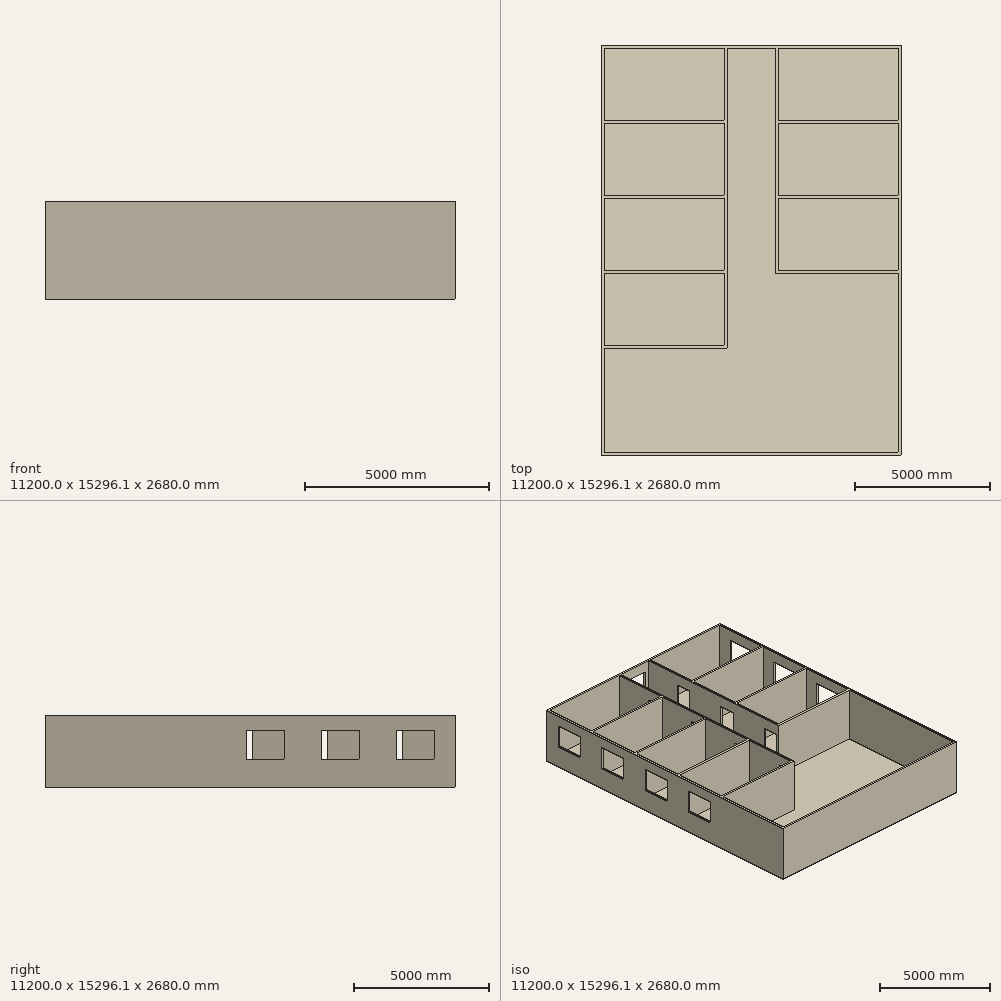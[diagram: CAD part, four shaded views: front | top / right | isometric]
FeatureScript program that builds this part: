
annotation { "Feature Type Name" : "Feature", "Feature Type Description" : "" }
export const myFeature = defineFeature(function(context is Context, id is Id, definition is map)
    precondition{}
    {
        {
            var Q0;
            Q0=qCreatedBy(makeId("Top.planeOp"),FACE);
            var sketch = newSketch(context, id + "F0", { "sketchPlane" : qUnion([Q0])});
            skLineSegment(sketch, "E0.bottom", {"start": v(4600, -100) * mm, "end": v(100, -100) * mm});
            skLineSegment(sketch, "E0.top", {"start": v(4600, -2800) * mm, "end": v(100, -2800) * mm});
            skLineSegment(sketch, "E0.left", {"start": v(4600, -100) * mm, "end": v(4600, -2800) * mm});
            skLineSegment(sketch, "E0.right", {"start": v(100, -100) * mm, "end": v(100, -2800) * mm});
            skLineSegment(sketch, "E1.bottom", {"start": v(4600, -2900) * mm, "end": v(100, -2900) * mm});
            skLineSegment(sketch, "E1.top", {"start": v(4600, -5600) * mm, "end": v(100, -5600) * mm});
            skLineSegment(sketch, "E1.left", {"start": v(4600, -2900) * mm, "end": v(4600, -5600) * mm});
            skLineSegment(sketch, "E1.right", {"start": v(100, -2900) * mm, "end": v(100, -5600) * mm});
            skLineSegment(sketch, "E2.bottom", {"start": v(11100, -100) * mm, "end": v(6600, -100) * mm});
            skLineSegment(sketch, "E2.top", {"start": v(11100, -2800) * mm, "end": v(6600, -2800) * mm});
            skLineSegment(sketch, "E2.left", {"start": v(11100, -100) * mm, "end": v(11100, -2800) * mm});
            skLineSegment(sketch, "E2.right", {"start": v(6600, -100) * mm, "end": v(6600, -2800) * mm});
            skLineSegment(sketch, "E3.bottom", {"start": v(11100, -2900) * mm, "end": v(6600, -2900) * mm});
            skLineSegment(sketch, "E3.top", {"start": v(11100, -5600) * mm, "end": v(6600, -5600) * mm});
            skLineSegment(sketch, "E3.left", {"start": v(11100, -2900) * mm, "end": v(11100, -5600) * mm});
            skLineSegment(sketch, "E3.right", {"start": v(6600, -2900) * mm, "end": v(6600, -5600) * mm});
            skLineSegment(sketch, "E4.bottom", {"start": v(4700, -100) * mm, "end": v(6500, -100) * mm});
            skLineSegment(sketch, "E5.bottom", {"start": v(0, 0) * mm, "end": v(11200, 0) * mm});
            skLineSegment(sketch, "E5.top", {"start": v(0, -15296.15) * mm, "end": v(11200, -15296.15) * mm});
            skLineSegment(sketch, "E5.left", {"start": v(0, 0) * mm, "end": v(0, -15296.15) * mm});
            skLineSegment(sketch, "E5.right", {"start": v(11200, 0) * mm, "end": v(11200, -15296.15) * mm});
            skLineSegment(sketch, "E6.bottom", {"start": v(4600, -5700) * mm, "end": v(100, -5700) * mm});
            skLineSegment(sketch, "E6.top", {"start": v(4600, -8400) * mm, "end": v(100, -8400) * mm});
            skLineSegment(sketch, "E6.left", {"start": v(4600, -5700) * mm, "end": v(4600, -8400) * mm});
            skLineSegment(sketch, "E6.right", {"start": v(100, -5700) * mm, "end": v(100, -8400) * mm});
            skLineSegment(sketch, "E7.bottom", {"start": v(11100, -5700) * mm, "end": v(6600, -5700) * mm});
            skLineSegment(sketch, "E7.top", {"start": v(11100, -8400) * mm, "end": v(6600, -8400) * mm});
            skLineSegment(sketch, "E7.left", {"start": v(11100, -5700) * mm, "end": v(11100, -8400) * mm});
            skLineSegment(sketch, "E7.right", {"start": v(6600, -5700) * mm, "end": v(6600, -8400) * mm});
            skLineSegment(sketch, "E8.bottom", {"start": v(4600, -8500) * mm, "end": v(100, -8500) * mm});
            skLineSegment(sketch, "E8.top", {"start": v(4600, -11200) * mm, "end": v(100, -11200) * mm});
            skLineSegment(sketch, "E8.left", {"start": v(4600, -8500) * mm, "end": v(4600, -11200) * mm});
            skLineSegment(sketch, "E8.right", {"start": v(100, -8500) * mm, "end": v(100, -11200) * mm});
            skLineSegment(sketch, "E9", {"start": v(6500, -8500) * mm, "end": v(6500, -100) * mm});
            skLineSegment(sketch, "E10", {"start": v(4700, -11300) * mm, "end": v(4700, -100) * mm});
            skLineSegment(sketch, "E11", {"start": v(6500, -8500) * mm, "end": v(11100, -8500) * mm});
            skLineSegment(sketch, "E12", {"start": v(11100, -8500) * mm, "end": v(11100, -15196.15) * mm});
            skLineSegment(sketch, "E13", {"start": v(11100, -15196.15) * mm, "end": v(100, -15196.15) * mm});
            skLineSegment(sketch, "E14", {"start": v(100, -15196.15) * mm, "end": v(100, -11300) * mm});
            skLineSegment(sketch, "E15", {"start": v(100, -11300) * mm, "end": v(4700, -11300) * mm});
            skLineSegment(sketch, "E16.bottom", {"start": v(4600, -2760) * mm, "end": v(4700, -2760) * mm});
            skLineSegment(sketch, "E16.top", {"start": v(4600, -1960) * mm, "end": v(4700, -1960) * mm});
            skLineSegment(sketch, "E16.left", {"start": v(4600, -2760) * mm, "end": v(4600, -1960) * mm});
            skLineSegment(sketch, "E16.right", {"start": v(4700, -2760) * mm, "end": v(4700, -1960) * mm});
            skLineSegment(sketch, "E17.bottom", {"start": v(6500, -2760) * mm, "end": v(6600, -2760) * mm});
            skLineSegment(sketch, "E17.top", {"start": v(6500, -1960) * mm, "end": v(6600, -1960) * mm});
            skLineSegment(sketch, "E17.left", {"start": v(6500, -2760) * mm, "end": v(6500, -1960) * mm});
            skLineSegment(sketch, "E17.right", {"start": v(6600, -2760) * mm, "end": v(6600, -1960) * mm});
            skLineSegment(sketch, "E18.bottom", {"start": v(6500, -5560) * mm, "end": v(6600, -5560) * mm});
            skLineSegment(sketch, "E18.top", {"start": v(6500, -4760) * mm, "end": v(6600, -4760) * mm});
            skLineSegment(sketch, "E18.left", {"start": v(6500, -5560) * mm, "end": v(6500, -4760) * mm});
            skLineSegment(sketch, "E18.right", {"start": v(6600, -5560) * mm, "end": v(6600, -4760) * mm});
            skLineSegment(sketch, "E19.bottom", {"start": v(4600, -5560) * mm, "end": v(4700, -5560) * mm});
            skLineSegment(sketch, "E19.top", {"start": v(4600, -4760) * mm, "end": v(4700, -4760) * mm});
            skLineSegment(sketch, "E19.left", {"start": v(4600, -5560) * mm, "end": v(4600, -4760) * mm});
            skLineSegment(sketch, "E19.right", {"start": v(4700, -5560) * mm, "end": v(4700, -4760) * mm});
            skLineSegment(sketch, "E20.bottom", {"start": v(4600, -8360) * mm, "end": v(4700, -8360) * mm});
            skLineSegment(sketch, "E20.top", {"start": v(4600, -7560) * mm, "end": v(4700, -7560) * mm});
            skLineSegment(sketch, "E20.left", {"start": v(4600, -8360) * mm, "end": v(4600, -7560) * mm});
            skLineSegment(sketch, "E20.right", {"start": v(4700, -8360) * mm, "end": v(4700, -7560) * mm});
            skLineSegment(sketch, "E21.bottom", {"start": v(6500, -8360) * mm, "end": v(6600, -8360) * mm});
            skLineSegment(sketch, "E21.top", {"start": v(6500, -7560) * mm, "end": v(6600, -7560) * mm});
            skLineSegment(sketch, "E21.left", {"start": v(6500, -8360) * mm, "end": v(6500, -7560) * mm});
            skLineSegment(sketch, "E21.right", {"start": v(6600, -8360) * mm, "end": v(6600, -7560) * mm});
            skLineSegment(sketch, "E22.bottom", {"start": v(4600, -11240) * mm, "end": v(4700, -11240) * mm});
            skLineSegment(sketch, "E22.top", {"start": v(4600, -10440) * mm, "end": v(4700, -10440) * mm});
            skLineSegment(sketch, "E22.left", {"start": v(4600, -11240) * mm, "end": v(4600, -10440) * mm});
            skLineSegment(sketch, "E22.right", {"start": v(4700, -11240) * mm, "end": v(4700, -10440) * mm});
            skSolve(sketch);
        }
        {
            var Q0;
            {var subQ38=sQuery(id+"F0.wireOp",EDGE,"E0.bottom");Q0=makeQuery(id+"F0.imprint","IMPRINT",FACE,{"disambiguationData":[TD([[makeQuery(id+"F0.imprint","IMPRINT",EDGE,{"derivedFrom":subQ38}),-1.0]])]});}
            extrude(context, id + "F1", {"entities" : qUnion([Q0]), "oppositeDirection" : true, "depth" : 2050 * mm, "offsetDistance" : 25 * mm});
        }
        {
            var Q0;
            {var subQ38=sQuery(id+"F0.wireOp",EDGE,"E0.bottom");Q0=makeQuery(id+"F0.imprint","IMPRINT",FACE,{"disambiguationData":[TD([[makeQuery(id+"F0.imprint","IMPRINT",EDGE,{"derivedFrom":subQ38}),-1.0]])]});}
            var Q1;
            Q1=makeQuery(id+"F0.imprint","IMPRINT",FACE,{"disambiguationData":[TD([[makeQuery(id+"F0.imprint","IMPRINT",EDGE,{"derivedFrom":sQuery(id+"F0.wireOp",EDGE,"E17.bottom")}),1.0]])]});
            var Q2;
            Q2=makeQuery(id+"F0.imprint","IMPRINT",FACE,{"disambiguationData":[TD([[makeQuery(id+"F0.imprint","IMPRINT",EDGE,{"derivedFrom":sQuery(id+"F0.wireOp",EDGE,"E18.bottom")}),1.0]])]});
            var Q3;
            Q3=makeQuery(id+"F0.imprint","IMPRINT",FACE,{"disambiguationData":[TD([[makeQuery(id+"F0.imprint","IMPRINT",EDGE,{"derivedFrom":sQuery(id+"F0.wireOp",EDGE,"E22.bottom")}),1.0]])]});
            var Q4;
            Q4=makeQuery(id+"F0.imprint","IMPRINT",FACE,{"disambiguationData":[TD([[makeQuery(id+"F0.imprint","IMPRINT",EDGE,{"derivedFrom":sQuery(id+"F0.wireOp",EDGE,"E21.bottom")}),1.0]])]});
            var Q5;
            Q5=makeQuery(id+"F0.imprint","IMPRINT",FACE,{"disambiguationData":[TD([[makeQuery(id+"F0.imprint","IMPRINT",EDGE,{"derivedFrom":sQuery(id+"F0.wireOp",EDGE,"E20.bottom")}),1.0]])]});
            var Q6;
            Q6=makeQuery(id+"F0.imprint","IMPRINT",FACE,{"disambiguationData":[TD([[makeQuery(id+"F0.imprint","IMPRINT",EDGE,{"derivedFrom":sQuery(id+"F0.wireOp",EDGE,"E19.bottom")}),1.0]])]});
            var Q7;
            Q7=makeQuery(id+"F0.imprint","IMPRINT",FACE,{"disambiguationData":[TD([[makeQuery(id+"F0.imprint","IMPRINT",EDGE,{"derivedFrom":sQuery(id+"F0.wireOp",EDGE,"E16.bottom")}),1.0]])]});
            extrude(context, id + "F2", {"entities" : qUnion([Q0, Q1, Q2, Q3, Q4, Q5, Q6, Q7]), "operationType" : NewBodyOperationType.ADD, "depth" : 530 * mm, "offsetDistance" : 25 * mm});
        }
        {
            var Q0;
            Q0=makeQuery(id+"F1.opExtrude","CAP_FACE",FACE,{"disambiguationData":[OSD([sQuery(id+"F0.wireOp",EDGE,"E0.bottom"),sQuery(id+"F0.wireOp",EDGE,"E0.top"),sQuery(id+"F0.wireOp",EDGE,"E0.left"),sQuery(id+"F0.wireOp",EDGE,"E0.right"),sQuery(id+"F0.wireOp",EDGE,"E1.bottom"),sQuery(id+"F0.wireOp",EDGE,"E1.top"),sQuery(id+"F0.wireOp",EDGE,"E1.left"),sQuery(id+"F0.wireOp",EDGE,"E1.right"),sQuery(id+"F0.wireOp",EDGE,"E2.bottom"),sQuery(id+"F0.wireOp",EDGE,"E2.top"),sQuery(id+"F0.wireOp",EDGE,"E2.left"),sQuery(id+"F0.wireOp",EDGE,"E2.right"),sQuery(id+"F0.wireOp",EDGE,"E3.bottom"),sQuery(id+"F0.wireOp",EDGE,"E3.top"),sQuery(id+"F0.wireOp",EDGE,"E3.left"),sQuery(id+"F0.wireOp",EDGE,"E3.right"),sQuery(id+"F0.wireOp",EDGE,"E4.bottom"),sQuery(id+"F0.wireOp",EDGE,"E5.bottom"),sQuery(id+"F0.wireOp",EDGE,"E5.top"),sQuery(id+"F0.wireOp",EDGE,"E5.left"),sQuery(id+"F0.wireOp",EDGE,"E5.right"),sQuery(id+"F0.wireOp",EDGE,"E6.bottom"),sQuery(id+"F0.wireOp",EDGE,"E6.top"),sQuery(id+"F0.wireOp",EDGE,"E6.left"),sQuery(id+"F0.wireOp",EDGE,"E6.right"),sQuery(id+"F0.wireOp",EDGE,"E7.bottom"),sQuery(id+"F0.wireOp",EDGE,"E7.top"),sQuery(id+"F0.wireOp",EDGE,"E7.left"),sQuery(id+"F0.wireOp",EDGE,"E7.right"),sQuery(id+"F0.wireOp",EDGE,"E8.bottom"),sQuery(id+"F0.wireOp",EDGE,"E8.top"),sQuery(id+"F0.wireOp",EDGE,"E8.left"),sQuery(id+"F0.wireOp",EDGE,"E8.right"),sQuery(id+"F0.wireOp",EDGE,"E9"),sQuery(id+"F0.wireOp",EDGE,"E10"),sQuery(id+"F0.wireOp",EDGE,"E11"),sQuery(id+"F0.wireOp",EDGE,"E12"),sQuery(id+"F0.wireOp",EDGE,"E13"),sQuery(id+"F0.wireOp",EDGE,"E14"),sQuery(id+"F0.wireOp",EDGE,"E15"),sQuery(id+"F0.wireOp",EDGE,"E16.bottom"),sQuery(id+"F0.wireOp",EDGE,"E16.top"),sQuery(id+"F0.wireOp",EDGE,"E17.bottom"),sQuery(id+"F0.wireOp",EDGE,"E17.top"),sQuery(id+"F0.wireOp",EDGE,"E18.bottom"),sQuery(id+"F0.wireOp",EDGE,"E18.top"),sQuery(id+"F0.wireOp",EDGE,"E19.bottom"),sQuery(id+"F0.wireOp",EDGE,"E19.top"),sQuery(id+"F0.wireOp",EDGE,"E20.bottom"),sQuery(id+"F0.wireOp",EDGE,"E20.top"),sQuery(id+"F0.wireOp",EDGE,"E21.bottom"),sQuery(id+"F0.wireOp",EDGE,"E21.top"),sQuery(id+"F0.wireOp",EDGE,"E22.bottom"),sQuery(id+"F0.wireOp",EDGE,"E22.top")])],"isStart":false});
            var sketch = newSketch(context, id + "F3", { "sketchPlane" : qUnion([Q0])});
            skLineSegment(sketch, "E23.bottom", {"start": v(11200, 0) * mm, "end": v(0, 0) * mm});
            skLineSegment(sketch, "E23.top", {"start": v(11200, 15296.15) * mm, "end": v(0, 15296.15) * mm});
            skLineSegment(sketch, "E23.left", {"start": v(11200, 0) * mm, "end": v(11200, 15296.15) * mm});
            skLineSegment(sketch, "E23.right", {"start": v(0, 0) * mm, "end": v(0, 15296.15) * mm});
            skSolve(sketch);
        }
        {
            var Q0;
            Q0 = qSketchRegion(id + "F3", true);
            extrude(context, id + "F4", {"entities" : qUnion([Q0]), "operationType" : NewBodyOperationType.ADD, "depth" : 100 * mm, "offsetDistance" : 25 * mm});
        }
        {
            var Q0;
            {var subQ0=sQuery(id+"F0.wireOp",EDGE,"E4.bottom");Q0=makeQuery(id+"F2.boolean.opBoolean","MERGE",FACE,{"derivedFrom":[makeQuery(id+"F1.opExtrude","SWEPT_FACE",FACE,{"disambiguationData":[OSD([subQ0])]}),makeQuery(id+"F2.opExtrude","SWEPT_FACE",FACE,{"disambiguationData":[OSD([subQ0])]})]});}
            var sketch = newSketch(context, id + "F5", { "sketchPlane" : qUnion([Q0])});
            skLineSegment(sketch, "E24.bottom", {"start": v(4900, 10) * mm, "end": v(6300, 10) * mm});
            skLineSegment(sketch, "E24.top", {"start": v(4900, -1100) * mm, "end": v(6300, -1100) * mm});
            skLineSegment(sketch, "E24.left", {"start": v(4900, 10) * mm, "end": v(4900, -1100) * mm});
            skLineSegment(sketch, "E24.right", {"start": v(6300, 10) * mm, "end": v(6300, -1100) * mm});
            skSolve(sketch);
        }
        {
            var Q0;
            Q0=makeQuery(id+"F5.imprint","IMPRINT",FACE,{"disambiguationData":[TD([[makeQuery(id+"F5.imprint","IMPRINT",EDGE,{"derivedFrom":sQuery(id+"F5.wireOp",EDGE,"E24.bottom")}),-1.0]])]});
            extrude(context, id + "F6", {"entities" : qUnion([Q0]), "operationType" : NewBodyOperationType.REMOVE, "endBound" : BoundingType.UP_TO_NEXT, "oppositeDirection" : true, "depth" : 25 * mm, "offsetDistance" : 25 * mm});
        }
        {
            var Q0;
            {var subQ0=sQuery(id+"F0.wireOp",EDGE,"E0.right");Q0=makeQuery(id+"F2.boolean.opBoolean","MERGE",FACE,{"derivedFrom":[makeQuery(id+"F1.opExtrude","SWEPT_FACE",FACE,{"disambiguationData":[OSD([subQ0])]}),makeQuery(id+"F2.opExtrude","SWEPT_FACE",FACE,{"disambiguationData":[OSD([subQ0])]})]});}
            var sketch = newSketch(context, id + "F7", { "sketchPlane" : qUnion([Q0])});
            skLineSegment(sketch, "E25.bottom", {"start": v(-2190, 10) * mm, "end": v(-770, 10) * mm});
            skLineSegment(sketch, "E25.top", {"start": v(-2190, -1100) * mm, "end": v(-770, -1100) * mm});
            skLineSegment(sketch, "E25.left", {"start": v(-2190, 10) * mm, "end": v(-2190, -1100) * mm});
            skLineSegment(sketch, "E25.right", {"start": v(-770, 10) * mm, "end": v(-770, -1100) * mm});
            skLineSegment(sketch, "E26.bottom", {"start": v(-3570, -1100) * mm, "end": v(-4990, -1100) * mm});
            skLineSegment(sketch, "E26.top", {"start": v(-3570, 10) * mm, "end": v(-4990, 10) * mm});
            skLineSegment(sketch, "E26.left", {"start": v(-3570, -1100) * mm, "end": v(-3570, 10) * mm});
            skLineSegment(sketch, "E26.right", {"start": v(-4990, -1100) * mm, "end": v(-4990, 10) * mm});
            skLineSegment(sketch, "E27.bottom", {"start": v(-6370, -1100) * mm, "end": v(-7790, -1100) * mm});
            skLineSegment(sketch, "E27.top", {"start": v(-6370, 10) * mm, "end": v(-7790, 10) * mm});
            skLineSegment(sketch, "E27.left", {"start": v(-6370, -1100) * mm, "end": v(-6370, 10) * mm});
            skLineSegment(sketch, "E27.right", {"start": v(-7790, -1100) * mm, "end": v(-7790, 10) * mm});
            skLineSegment(sketch, "E28.bottom", {"start": v(-9170, -1100) * mm, "end": v(-10590, -1100) * mm});
            skLineSegment(sketch, "E28.top", {"start": v(-9170, 10) * mm, "end": v(-10590, 10) * mm});
            skLineSegment(sketch, "E28.left", {"start": v(-9170, -1100) * mm, "end": v(-9170, 10) * mm});
            skLineSegment(sketch, "E28.right", {"start": v(-10590, -1100) * mm, "end": v(-10590, 10) * mm});
            skSolve(sketch);
        }
        {
            var Q0;
            Q0=makeQuery(id+"F7.imprint","IMPRINT",FACE,{"disambiguationData":[TD([[makeQuery(id+"F7.imprint","IMPRINT",EDGE,{"derivedFrom":sQuery(id+"F7.wireOp",EDGE,"E28.bottom")}),-1.0]])]});
            var Q1;
            Q1=makeQuery(id+"F7.imprint","IMPRINT",FACE,{"disambiguationData":[TD([[makeQuery(id+"F7.imprint","IMPRINT",EDGE,{"derivedFrom":sQuery(id+"F7.wireOp",EDGE,"E27.bottom")}),-1.0]])]});
            var Q2;
            Q2=makeQuery(id+"F7.imprint","IMPRINT",FACE,{"disambiguationData":[TD([[makeQuery(id+"F7.imprint","IMPRINT",EDGE,{"derivedFrom":sQuery(id+"F7.wireOp",EDGE,"E26.bottom")}),-1.0]])]});
            var Q3;
            Q3=makeQuery(id+"F7.imprint","IMPRINT",FACE,{"disambiguationData":[TD([[makeQuery(id+"F7.imprint","IMPRINT",EDGE,{"derivedFrom":sQuery(id+"F7.wireOp",EDGE,"E25.bottom")}),-1.0]])]});
            extrude(context, id + "F8", {"entities" : qUnion([Q0, Q1, Q2, Q3]), "operationType" : NewBodyOperationType.REMOVE, "endBound" : BoundingType.UP_TO_NEXT, "oppositeDirection" : true, "depth" : 25 * mm, "offsetDistance" : 25 * mm});
        }
        {
            var Q0;
            {var subQ0=sQuery(id+"F0.wireOp",EDGE,"E2.left");Q0=makeQuery(id+"F2.boolean.opBoolean","MERGE",FACE,{"derivedFrom":[makeQuery(id+"F1.opExtrude","SWEPT_FACE",FACE,{"disambiguationData":[OSD([subQ0])]}),makeQuery(id+"F2.opExtrude","SWEPT_FACE",FACE,{"disambiguationData":[OSD([subQ0])]})]});}
            var sketch = newSketch(context, id + "F9", { "sketchPlane" : qUnion([Q0])});
            skLineSegment(sketch, "E29.bottom", {"start": v(7790, -1100) * mm, "end": v(6370, -1100) * mm});
            skLineSegment(sketch, "E29.top", {"start": v(7790, -10) * mm, "end": v(6370, -10) * mm});
            skLineSegment(sketch, "E29.left", {"start": v(7790, -1100) * mm, "end": v(7790, -10) * mm});
            skLineSegment(sketch, "E29.right", {"start": v(6370, -1100) * mm, "end": v(6370, -10) * mm});
            skLineSegment(sketch, "E30.bottom", {"start": v(4990, -1100) * mm, "end": v(3570, -1100) * mm});
            skLineSegment(sketch, "E30.top", {"start": v(4990, -10) * mm, "end": v(3570, -10) * mm});
            skLineSegment(sketch, "E30.left", {"start": v(4990, -1100) * mm, "end": v(4990, -10) * mm});
            skLineSegment(sketch, "E30.right", {"start": v(3570, -1100) * mm, "end": v(3570, -10) * mm});
            skLineSegment(sketch, "E31.bottom", {"start": v(2190, -1100) * mm, "end": v(770, -1100) * mm});
            skLineSegment(sketch, "E31.top", {"start": v(2190, -10) * mm, "end": v(770, -10) * mm});
            skLineSegment(sketch, "E31.left", {"start": v(2190, -1100) * mm, "end": v(2190, -10) * mm});
            skLineSegment(sketch, "E31.right", {"start": v(770, -1100) * mm, "end": v(770, -10) * mm});
            skSolve(sketch);
        }
        {
            var Q0;
            Q0=makeQuery(id+"F9.imprint","IMPRINT",FACE,{"disambiguationData":[TD([[makeQuery(id+"F9.imprint","IMPRINT",EDGE,{"derivedFrom":sQuery(id+"F9.wireOp",EDGE,"E31.bottom")}),-1.0]])]});
            var Q1;
            Q1=makeQuery(id+"F9.imprint","IMPRINT",FACE,{"disambiguationData":[TD([[makeQuery(id+"F9.imprint","IMPRINT",EDGE,{"derivedFrom":sQuery(id+"F9.wireOp",EDGE,"E30.bottom")}),-1.0]])]});
            var Q2;
            Q2=makeQuery(id+"F9.imprint","IMPRINT",FACE,{"disambiguationData":[TD([[makeQuery(id+"F9.imprint","IMPRINT",EDGE,{"derivedFrom":sQuery(id+"F9.wireOp",EDGE,"E29.bottom")}),-1.0]])]});
            extrude(context, id + "F10", {"entities" : qUnion([Q0, Q1, Q2]), "operationType" : NewBodyOperationType.REMOVE, "endBound" : BoundingType.UP_TO_NEXT, "oppositeDirection" : true, "depth" : 25 * mm, "offsetDistance" : 25 * mm});
        }
    });
